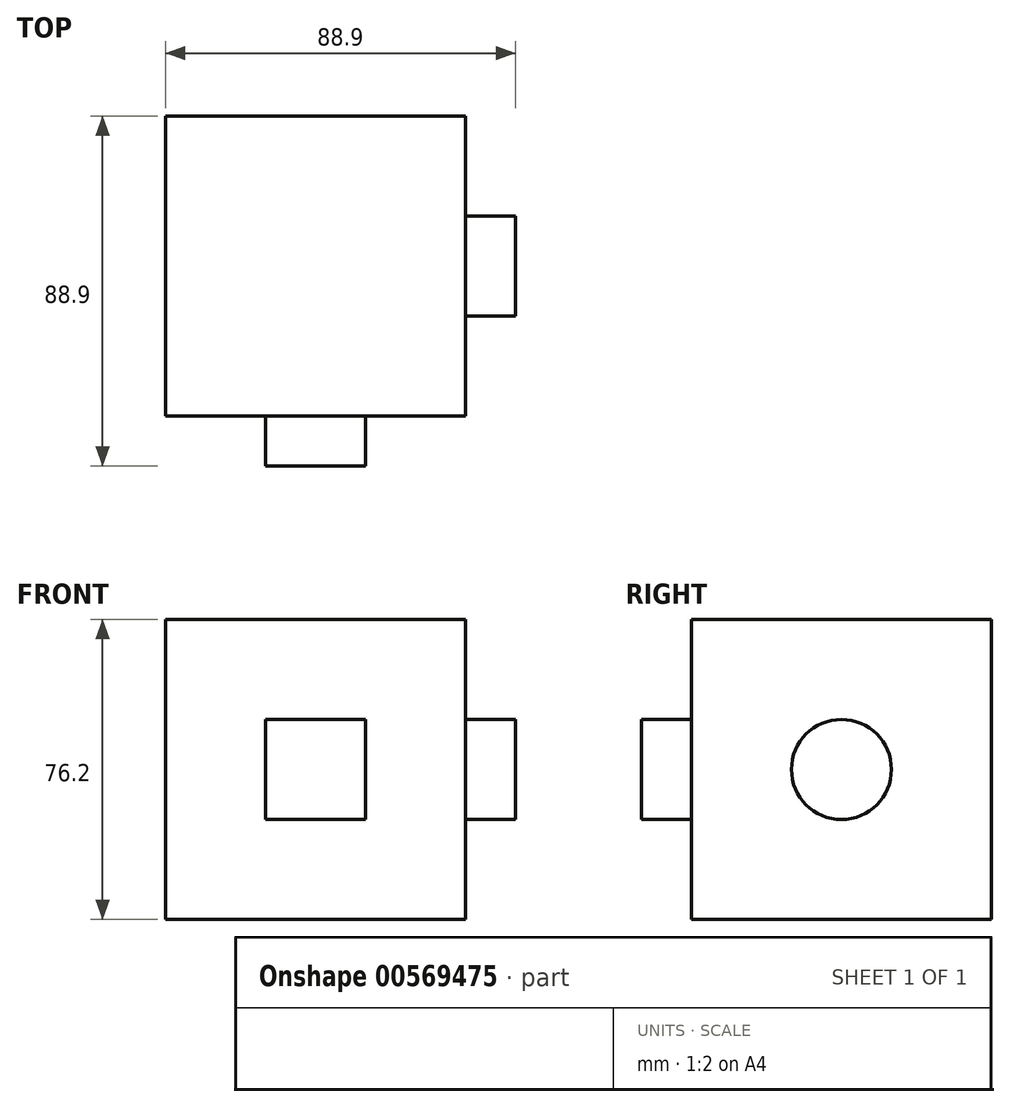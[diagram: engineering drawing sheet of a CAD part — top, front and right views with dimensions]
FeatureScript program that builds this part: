
annotation { "Feature Type Name" : "Feature", "Feature Type Description" : "" }
export const myFeature = defineFeature(function(context is Context, id is Id, definition is map)
    precondition{}
    {
        {
            var Q0;
            Q0=qCreatedBy(makeId("Front.planeOp"),FACE);
            var sketch = newSketch(context, id + "F0", { "sketchPlane" : qUnion([Q0])});
            skLineSegment(sketch, "E0.bottom", {"start": v(-144.47, 119.43) * mm, "end": v(-68.27, 119.43) * mm});
            skLineSegment(sketch, "E0.top", {"start": v(-144.47, 43.23) * mm, "end": v(-68.27, 43.23) * mm});
            skLineSegment(sketch, "E0.left", {"start": v(-144.47, 119.43) * mm, "end": v(-144.47, 43.23) * mm});
            skLineSegment(sketch, "E0.right", {"start": v(-68.27, 119.43) * mm, "end": v(-68.27, 43.23) * mm});
            skSolve(sketch);
        }
        {
            var Q0;
            Q0=makeQuery(id+"F0.imprint","IMPRINT",FACE,{"disambiguationData":[TD([[makeQuery(id+"F0.imprint","IMPRINT",EDGE,{"derivedFrom":sQuery(id+"F0.wireOp",EDGE,"E0.bottom")}),-1.0]])]});
            extrude(context, id + "F1", {"entities" : qUnion([Q0]), "depth" : 76.2 * mm, "offsetDistance" : 25.4 * mm});
        }
        {
            var Q0;
            Q0=makeQuery(id+"F1.opExtrude","CAP_FACE",FACE,{"disambiguationData":[OSD([sQuery(id+"F0.wireOp",EDGE,"E0.bottom"),sQuery(id+"F0.wireOp",EDGE,"E0.top"),sQuery(id+"F0.wireOp",EDGE,"E0.left"),sQuery(id+"F0.wireOp",EDGE,"E0.right")])],"isStart":false});
            var sketch = newSketch(context, id + "F2", { "sketchPlane" : qUnion([Q0])});
            skLineSegment(sketch, "E1.bottom", {"start": v(-119.07, 94.03) * mm, "end": v(-93.67, 94.03) * mm});
            skLineSegment(sketch, "E1.top", {"start": v(-119.07, 68.63) * mm, "end": v(-93.67, 68.63) * mm});
            skLineSegment(sketch, "E1.left", {"start": v(-119.07, 94.03) * mm, "end": v(-119.07, 68.63) * mm});
            skLineSegment(sketch, "E1.right", {"start": v(-93.67, 94.03) * mm, "end": v(-93.67, 68.63) * mm});
            skSolve(sketch);
        }
        {
            var Q0;
            Q0=makeQuery(id+"F2.imprint","IMPRINT",FACE,{"disambiguationData":[TD([[makeQuery(id+"F2.imprint","IMPRINT",EDGE,{"derivedFrom":sQuery(id+"F2.wireOp",EDGE,"E1.bottom")}),-1.0]])]});
            extrude(context, id + "F3", {"entities" : qUnion([Q0]), "operationType" : NewBodyOperationType.ADD, "depth" : 12.7 * mm, "offsetDistance" : 25.4 * mm});
        }
        {
            var Q0;
            Q0=makeQuery(id+"F1.opExtrude","SWEPT_FACE",FACE,{"disambiguationData":[OSD([sQuery(id+"F0.wireOp",EDGE,"E0.right")])]});
            var sketch = newSketch(context, id + "F4", { "sketchPlane" : qUnion([Q0])});
            skCircle(sketch, "E2", {"center": v(-38.1, 81.33) * mm, "radius": 12.7 * mm});
            skSolve(sketch);
        }
        {
            var Q0;
            Q0=makeQuery(id+"F4.imprint","IMPRINT",FACE,{"disambiguationData":[TD([[makeQuery(id+"F4.imprint","IMPRINT",EDGE,{"derivedFrom":sQuery(id+"F4.wireOp",EDGE,"E2")}),1.0]])]});
            extrude(context, id + "F5", {"entities" : qUnion([Q0]), "operationType" : NewBodyOperationType.ADD, "depth" : 12.7 * mm, "offsetDistance" : 25.4 * mm});
        }
    });
